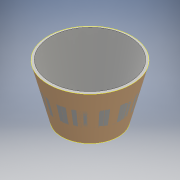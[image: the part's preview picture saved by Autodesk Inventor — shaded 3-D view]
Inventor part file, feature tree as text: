
AUTODESK INVENTOR PART (.ipt)
format: ipt  version: 2016 (Build 200138000, 138)  size: 118,784 bytes
history: native  units: mm
features: sketch x2, plane x1, thicken_offset x1, other x1, loft x1
ambient origin geometry x8: Origin, YZ Plane, XZ Plane, XY Plane, X Axis, Y Axis, Z Axis, Center Point
bodies: Body1 (feature_tree), Body2 (feature_tree)
feature tree (6):
  sketch  "Sketch1"  dims[d0=324.0mm d1=9.52mm]
  plane  "Work Plane1"
  thicken_offset  "Thicken1"
  sketch  "Sketch2"  dims[d2=-203.0mm d3=219.0mm d4=9.52mm d15=0.0mm d16=90.0deg d17=0.0mm d18=90.0deg d19=9.52mm d20=9.52mm]
  other  "Srf1"
  loft  "LoftSrf1"
